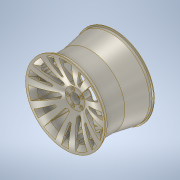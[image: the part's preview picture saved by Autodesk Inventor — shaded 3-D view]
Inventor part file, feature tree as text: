
AUTODESK INVENTOR PART (.ipt)
format: ipt  version: 2020.2 (Build 242310000, 310)  size: 743,936 bytes
history: native  units: in
note: dims shown in document units (in); Inventor stores cm internally (conversion verified against a paired STEP export)
features: sketch x7, extrude x7, chamfer x4, pattern_circular x3, revolve x1, plane x1, fillet x1
ambient origin geometry x8: Origin, YZ Plane, XZ Plane, XY Plane, X Axis, Y Axis, Z Axis, Center Point
bodies: Solid1 (feature_tree)
feature tree (24):
  revolve  "Revolution1"  [1 undecoded]
  plane  "Work Plane1"
  sketch  "Sketch2"  dims[d5=0.25in d6=0.7559in]
  extrude  "Extrusion1"  Depth=0.7559in
  chamfer  "Chamfer1"  Distance=0.5in
  sketch  "Sketch8"  dims[d10=0.75in]
  extrude  "Extrusion7"  Depth=2.0in
  pattern_circular  "Circular Pattern1"  [2 undecoded]
  extrude  "Extrusion6"  Depth=0.5in
  chamfer  "Chamfer4"  Distance=0.25in
  sketch  "Sketch9"  dims[d11=0.8589in d14=0.5in d15=2.0in d16=1.5in d18=0.5in d19=0.25in d20=0.75in d22=0.8589in d24=2.0in d25=2.0in d28=1.5in d29=1.0in d30=1.9in d31=0.6in d32=0.716in d33=90.0deg d34=5.0in d35=0.1718in d36=1.0in d43=1.25in d44=1.0in d45=0.0in d48=0.8in d49=0.125in d50=45.0deg d51=2.7559in d52=360.0deg d56=0.6in d58=1.5in d59=0.0in d60=0.5in d61=0.0in d62=0.35in d63=0.5in d64=0.0in d65=0.1in d66=0.125in d67=45.0deg d68=1.9685in d69=360.0deg d71=2.0in d72=0.5in d73=0.0in d74=0.1in d75=0.2in d76=0.125in d77=45.0deg d79=0.1374in d80=0.5in d81=3.0in d97=0.25in d98=4.0in d99=15.0deg d100=9.0in d101=0.0in d102=0.8in d103=0.125in d104=45.0deg d105=2.7559in d106=360.0deg d109=0.1718in d110=0.5in d111=8.0in d112=0.5in d115=6.0in d116=0.0in d118=0.5in d121=2.5in d122=6.0in d123=0.0in]
  extrude  "Extrusion8"  Depth=0.5in
  pattern_circular  "Circular Pattern4"  [2 undecoded]
  extrude  "Extrusion2"  Depth=2.0in
  extrude  "Extrusion3"  Depth=2.0in
  chamfer  "Chamfer2"  Distance=1.5in
  pattern_circular  "Circular Pattern2"  [2 undecoded]
  extrude  "Extrusion4"  Depth=0.5in
  fillet  "Fillet3"  Radius=0.6in
  chamfer  "Chamfer3"  Distance=0.716in
  sketch  "Sketch1"  dims[d2=15.0in d3=15.0in]
  sketch  "Sketch3"  dims[d7=0.125in]
  sketch  "Sketch4"  dims[d8=0.125in]
  sketch  "Sketch5"  dims[d9=0.7559in]
note: 7 required parameter values undecoded (feature->parameter linkage not recoverable at this tier; creation-order binding heuristic only, values carry confidence <= 0.55)